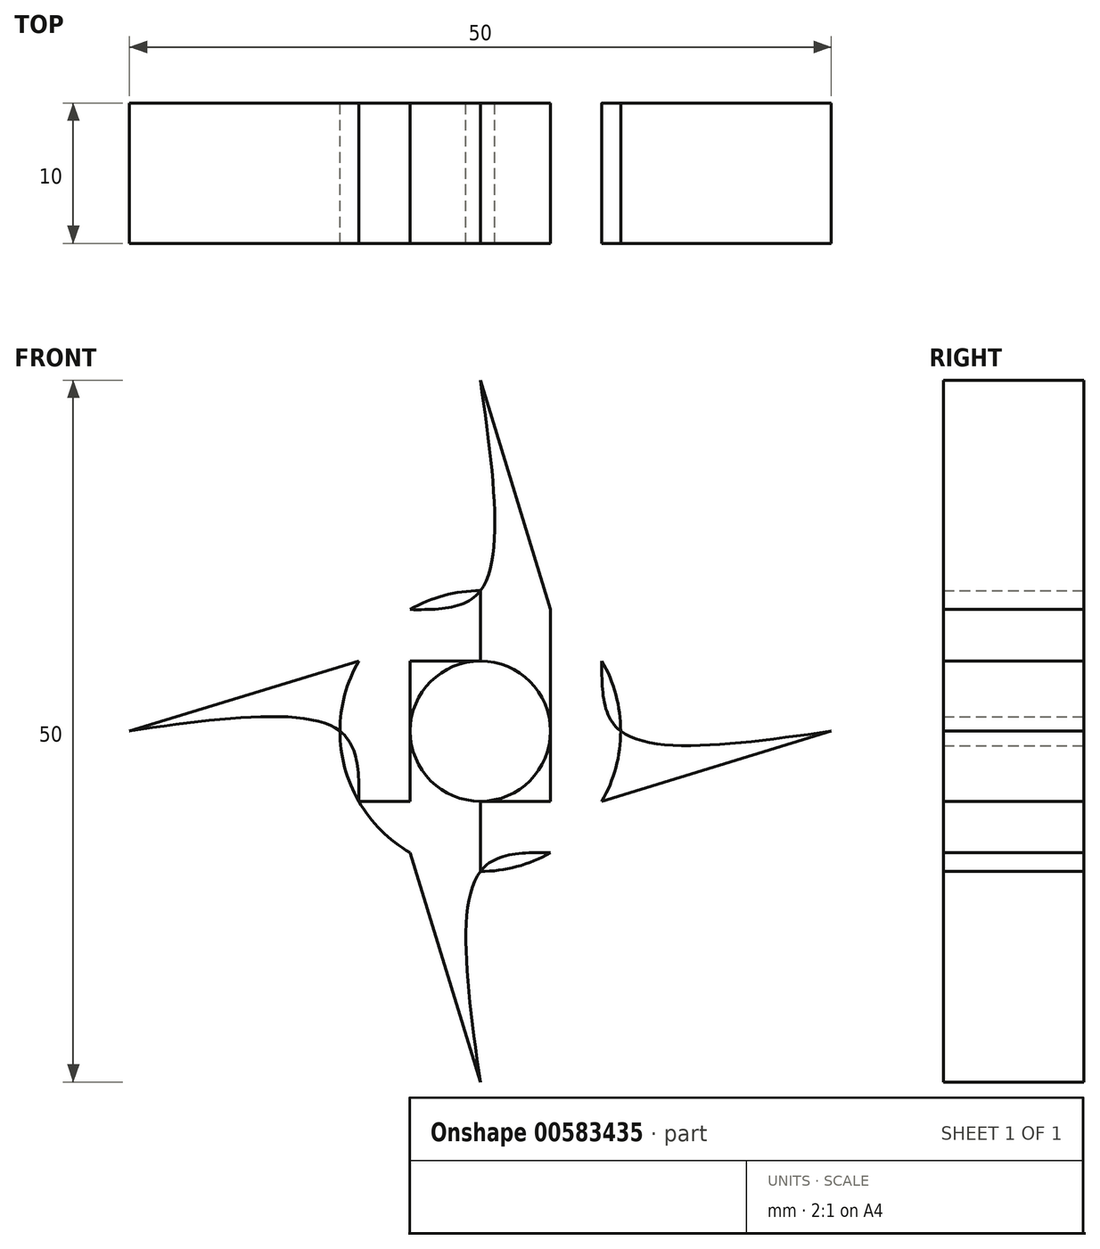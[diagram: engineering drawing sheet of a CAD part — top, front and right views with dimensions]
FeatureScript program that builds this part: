
annotation { "Feature Type Name" : "Feature", "Feature Type Description" : "" }
export const myFeature = defineFeature(function(context is Context, id is Id, definition is map)
    precondition{}
    {
        {
            var Q0;
            Q0=qCreatedBy(makeId("Front.planeOp"),FACE);
            var sketch = newSketch(context, id + "F0", { "sketchPlane" : qUnion([Q0])});
            skCircle(sketch, "E0", {"center": v(0, 0) * mm, "radius": 10 * mm});
            skLineSegment(sketch, "E1", {"start": v(0, 0) * mm, "end": v(0, 10) * mm});
            skLineSegment(sketch, "E2", {"start": v(0, 10) * mm, "end": v(0, -10) * mm});
            skLineSegment(sketch, "E3", {"start": v(-10, 0) * mm, "end": v(10, 0) * mm});
            skLineSegment(sketch, "E4", {"start": v(0, 0) * mm, "end": v(0, -10) * mm});
            skLineSegment(sketch, "E5", {"start": v(0, 0) * mm, "end": v(-10, 0) * mm});
            skLineSegment(sketch, "E6", {"start": v(0, 0) * mm, "end": v(10, 0) * mm});
            skLineSegment(sketch, "E7", {"start": v(0, 5) * mm, "end": v(-8.66, 5) * mm});
            skLineSegment(sketch, "E8", {"start": v(-8.66, 5) * mm, "end": v(8.66, 5) * mm});
            skLineSegment(sketch, "E9", {"start": v(0, -5) * mm, "end": v(8.66, -5) * mm});
            skLineSegment(sketch, "E10", {"start": v(8.66, -5) * mm, "end": v(-8.66, -5) * mm});
            skLineSegment(sketch, "E11", {"start": v(-5, 0) * mm, "end": v(-5, 8.66) * mm});
            skLineSegment(sketch, "E12", {"start": v(-5, 8.66) * mm, "end": v(-5, -8.66) * mm});
            skLineSegment(sketch, "E13", {"start": v(5, 0) * mm, "end": v(5, 8.66) * mm});
            skLineSegment(sketch, "E14", {"start": v(5, 8.66) * mm, "end": v(5, -8.66) * mm});
            skLineSegment(sketch, "E15", {"start": v(-8.66, 5) * mm, "end": v(-5, 5) * mm});
            skLineSegment(sketch, "E16", {"start": v(-5, 5) * mm, "end": v(-5, -5) * mm});
            skLineSegment(sketch, "E17", {"start": v(5, 5) * mm, "end": v(5, -5) * mm});
            skLineSegment(sketch, "E18.bottom", {"start": v(-5, -5) * mm, "end": v(4.96, -5) * mm});
            skLineSegment(sketch, "E19.left", {"start": v(-5, 5) * mm, "end": v(-5, -4.96) * mm});
            skLineSegment(sketch, "E20.bottom", {"start": v(-5, 5) * mm, "end": v(4.96, 5) * mm});
            skLineSegment(sketch, "E21.left", {"start": v(5, 5) * mm, "end": v(5, -4.96) * mm});
            skCircle(sketch, "E22", {"center": v(0, 0) * mm, "radius": 5 * mm});
            skLineSegment(sketch, "E23", {"start": v(25, 0) * mm, "end": v(8.66, -5) * mm});
            skLineSegment(sketch, "E24", {"start": v(-5, -8.66) * mm, "end": v(0, -25) * mm});
            skLineSegment(sketch, "E25", {"start": v(-8.66, 5) * mm, "end": v(-25, 0.02) * mm});
            skLineSegment(sketch, "E26", {"start": v(5, 8.66) * mm, "end": v(0, 25) * mm});
            skFitSpline(sketch, "E27", {"points": [v(0, 25) * mm, v(0, 10) * mm, v(-5, 8.66) * mm], "startDerivative": vector(4.26, -30.17) * mm, "endDerivative": vector(-16.01, 0.12) * mm});
            skFitSpline(sketch, "E28", {"points": [v(25, 0) * mm, v(10, 0) * mm, v(8.66, 5) * mm], "startDerivative": vector(-30.17, -4.26) * mm, "endDerivative": vector(0.12, 16.01) * mm});
            skFitSpline(sketch, "E29", {"points": [v(0, -25) * mm, v(0, -10) * mm, v(5, -8.66) * mm], "startDerivative": vector(-4.26, 30.17) * mm, "endDerivative": vector(16.01, -0.12) * mm});
            skFitSpline(sketch, "E30", {"points": [v(-25, 0.02) * mm, v(-10, 0) * mm, v(-8.66, -5) * mm], "startDerivative": vector(30.17, 4.21) * mm, "endDerivative": vector(-0.12, -16) * mm});
            skSolve(sketch);
        }
        {
            var Q0;
            {var subQ0=sQuery(id+"F0.wireOp",EDGE,"E4");var subQ1=sQuery(id+"F0.wireOp",EDGE,"E0");var subQ2=makeQuery(id+"F0.imprint","INTERSECT",VERTEX,{"derivedFrom":[subQ1,subQ0,sQuery(id+"F0.wireOp",EDGE,"ecfeab35-740d-4c83-b78b-e443c0464c7e")]});Q0=makeQuery(id+"F0.imprint","IMPRINT",FACE,{"disambiguationData":[TD([[makeQuery(id+"F0.imprint","IMPRINT",EDGE,{"disambiguationData":[TD([[subQ2,1.0]])],"derivedFrom":subQ1}),1.0]])]});}
            var Q1;
            {var subQ0=sQuery(id+"F0.wireOp",EDGE,"ecfeab35-740d-4c83-b78b-e443c0464c7e");var subQ1=sQuery(id+"F0.wireOp",EDGE,"E4");var subQ2=sQuery(id+"F0.wireOp",EDGE,"E0");var subQ3=makeQuery(id+"F0.imprint","INTERSECT",VERTEX,{"derivedFrom":[subQ2,subQ1,subQ0]});Q1=makeQuery(id+"F0.imprint","IMPRINT",FACE,{"disambiguationData":[TD([[makeQuery(id+"F0.imprint","IMPRINT",EDGE,{"disambiguationData":[TD([[subQ3,1.0]])],"derivedFrom":subQ1}),1.0]])]});}
            var Q2;
            {var subQ0=sQuery(id+"F0.wireOp",EDGE,"E10");var subQ1=sQuery(id+"F0.wireOp",EDGE,"E0");var subQ2=makeQuery(id+"F0.imprint","INTERSECT",VERTEX,{"derivedFrom":[subQ1,subQ0,sQuery(id+"F0.wireOp",EDGE,"sRVM3hvw-lM5L-FAK7-h2Cm-fDXYcMHcet7f")]});Q2=makeQuery(id+"F0.imprint","IMPRINT",FACE,{"disambiguationData":[TD([[makeQuery(id+"F0.imprint","IMPRINT",EDGE,{"disambiguationData":[TD([[subQ2,1.0]])],"derivedFrom":subQ1}),1.0]])]});}
            var Q3;
            {var subQ0=sQuery(id+"F0.wireOp",EDGE,"E6");var subQ1=sQuery(id+"F0.wireOp",EDGE,"E0");var subQ2=makeQuery(id+"F0.imprint","INTERSECT",VERTEX,{"derivedFrom":[subQ1,subQ0,sQuery(id+"F0.wireOp",EDGE,"dcaebb9e-91c8-481a-8361-05b1eb6cbfa7")]});Q3=makeQuery(id+"F0.imprint","IMPRINT",FACE,{"disambiguationData":[TD([[makeQuery(id+"F0.imprint","IMPRINT",EDGE,{"disambiguationData":[TD([[subQ2,1.0]])],"derivedFrom":subQ1}),1.0]])]});}
            var Q4;
            {var subQ6=sQuery(id+"F0.wireOp",EDGE,"E8");Q4=makeQuery(id+"F0.imprint","IMPRINT",FACE,{"disambiguationData":[TD([[makeQuery(id+"F0.imprint","IMPRINT",EDGE,{"derivedFrom":subQ6}),-1.0]])]});}
            var Q5;
            {var subQ0=sQuery(id+"F0.wireOp",EDGE,"E8");Q5=makeQuery(id+"F0.imprint","IMPRINT",FACE,{"disambiguationData":[TD([[makeQuery(id+"F0.imprint","IMPRINT",EDGE,{"derivedFrom":subQ0}),1.0]])]});}
            var Q6;
            {var subQ0=sQuery(id+"F0.wireOp",EDGE,"E2");var subQ1=sQuery(id+"F0.wireOp",EDGE,"E0");var subQ2=makeQuery(id+"F0.imprint","INTERSECT",VERTEX,{"derivedFrom":[subQ1,subQ0,sQuery(id+"F0.wireOp",EDGE,"3b5c119a-1b97-4d2e-8cfb-29280de54832")]});Q6=makeQuery(id+"F0.imprint","IMPRINT",FACE,{"disambiguationData":[TD([[makeQuery(id+"F0.imprint","IMPRINT",EDGE,{"disambiguationData":[TD([[subQ2,1.0]])],"derivedFrom":subQ1}),1.0]])]});}
            var Q7;
            {var subQ0=sQuery(id+"F0.wireOp",EDGE,"3b5c119a-1b97-4d2e-8cfb-29280de54832");var subQ1=sQuery(id+"F0.wireOp",EDGE,"E2");var subQ2=sQuery(id+"F0.wireOp",EDGE,"E0");var subQ3=makeQuery(id+"F0.imprint","INTERSECT",VERTEX,{"derivedFrom":[subQ2,subQ1,subQ0]});Q7=makeQuery(id+"F0.imprint","IMPRINT",FACE,{"disambiguationData":[TD([[makeQuery(id+"F0.imprint","IMPRINT",EDGE,{"disambiguationData":[TD([[subQ3,-1.0]])],"derivedFrom":subQ1}),-1.0]])]});}
            var Q8;
            {var subQ3=sQuery(id+"F0.wireOp",EDGE,"E15");Q8=makeQuery(id+"F0.imprint","IMPRINT",FACE,{"disambiguationData":[TD([[makeQuery(id+"F0.imprint","IMPRINT",EDGE,{"derivedFrom":subQ3}),-1.0]])]});}
            var Q9;
            {var subQ0=sQuery(id+"F0.wireOp",EDGE,"a55a1d35-224c-42bd-bfe0-43a0404cdbfa");var subQ1=sQuery(id+"F0.wireOp",EDGE,"E5");var subQ2=sQuery(id+"F0.wireOp",EDGE,"E0");var subQ3=makeQuery(id+"F0.imprint","INTERSECT",VERTEX,{"derivedFrom":[subQ2,subQ1,subQ0]});Q9=makeQuery(id+"F0.imprint","IMPRINT",FACE,{"disambiguationData":[TD([[makeQuery(id+"F0.imprint","IMPRINT",EDGE,{"disambiguationData":[TD([[subQ3,1.0]])],"derivedFrom":subQ1}),1.0]])]});}
            var Q10;
            {var subQ0=sQuery(id+"F0.wireOp",EDGE,"E10");var subQ1=sQuery(id+"F0.wireOp",EDGE,"E0");var subQ2=makeQuery(id+"F0.imprint","INTERSECT",VERTEX,{"derivedFrom":[subQ1,subQ0,sQuery(id+"F0.wireOp",EDGE,"a55a1d35-224c-42bd-bfe0-43a0404cdbfa")]});Q10=makeQuery(id+"F0.imprint","IMPRINT",FACE,{"disambiguationData":[TD([[makeQuery(id+"F0.imprint","IMPRINT",EDGE,{"disambiguationData":[TD([[subQ2,-1.0]])],"derivedFrom":subQ1}),1.0]])]});}
            var Q11;
            {var subQ3=sQuery(id+"F0.wireOp",EDGE,"E15");Q11=makeQuery(id+"F0.imprint","IMPRINT",FACE,{"disambiguationData":[TD([[makeQuery(id+"F0.imprint","IMPRINT",EDGE,{"derivedFrom":subQ3}),1.0]])]});}
            var Q12;
            {var subQ0=sQuery(id+"F0.wireOp",EDGE,"ecfeab35-740d-4c83-b78b-e443c0464c7e");var subQ1=sQuery(id+"F0.wireOp",EDGE,"E0");var subQ2=makeQuery(id+"F0.imprint","INTERSECT",VERTEX,{"derivedFrom":[subQ1,sQuery(id+"F0.wireOp",EDGE,"E4"),subQ0]});Q12=makeQuery(id+"F0.imprint","IMPRINT",FACE,{"disambiguationData":[TD([[makeQuery(id+"F0.imprint","IMPRINT",EDGE,{"disambiguationData":[TD([[subQ2,-1.0]])],"derivedFrom":subQ1}),1.0]])]});}
            var Q13;
            {var subQ0=sQuery(id+"F0.wireOp",EDGE,"a55a1d35-224c-42bd-bfe0-43a0404cdbfa");var subQ1=sQuery(id+"F0.wireOp",EDGE,"E0");var subQ2=makeQuery(id+"F0.imprint","INTERSECT",VERTEX,{"derivedFrom":[subQ1,sQuery(id+"F0.wireOp",EDGE,"E5"),subQ0]});Q13=makeQuery(id+"F0.imprint","IMPRINT",FACE,{"disambiguationData":[TD([[makeQuery(id+"F0.imprint","IMPRINT",EDGE,{"disambiguationData":[TD([[subQ2,-1.0]])],"derivedFrom":subQ1}),1.0]])]});}
            var Q14;
            {var subQ0=sQuery(id+"F0.wireOp",EDGE,"dcaebb9e-91c8-481a-8361-05b1eb6cbfa7");var subQ1=sQuery(id+"F0.wireOp",EDGE,"E0");var subQ2=makeQuery(id+"F0.imprint","INTERSECT",VERTEX,{"derivedFrom":[subQ1,sQuery(id+"F0.wireOp",EDGE,"E6"),subQ0]});Q14=makeQuery(id+"F0.imprint","IMPRINT",FACE,{"disambiguationData":[TD([[makeQuery(id+"F0.imprint","IMPRINT",EDGE,{"disambiguationData":[TD([[subQ2,-1.0]])],"derivedFrom":subQ1}),1.0]])]});}
            var Q15;
            {var subQ0=sQuery(id+"F0.wireOp",EDGE,"3b5c119a-1b97-4d2e-8cfb-29280de54832");var subQ1=sQuery(id+"F0.wireOp",EDGE,"E0");var subQ2=makeQuery(id+"F0.imprint","INTERSECT",VERTEX,{"derivedFrom":[subQ1,sQuery(id+"F0.wireOp",EDGE,"E2"),subQ0]});Q15=makeQuery(id+"F0.imprint","IMPRINT",FACE,{"disambiguationData":[TD([[makeQuery(id+"F0.imprint","IMPRINT",EDGE,{"disambiguationData":[TD([[subQ2,-1.0]])],"derivedFrom":subQ1}),1.0]])]});}
            var Q16;
            {var subQ1=sQuery(id+"F0.wireOp",EDGE,"E18.bottom");var subQ3=sQuery(id+"F0.wireOp",EDGE,"E22");var subQ4=makeQuery(id+"F0.imprint","INTERSECT",VERTEX,{"derivedFrom":[sQuery(id+"F0.wireOp",EDGE,"E4"),subQ1,subQ3]});Q16=makeQuery(id+"F0.imprint","IMPRINT",FACE,{"disambiguationData":[TD([[makeQuery(id+"F0.imprint","IMPRINT",EDGE,{"disambiguationData":[TD([[subQ4,1.0]])],"derivedFrom":subQ3}),-1.0]])]});}
            var Q17;
            {var subQ0=sQuery(id+"F0.wireOp",EDGE,"E20.bottom");var subQ3=sQuery(id+"F0.wireOp",EDGE,"E22");var subQ5=makeQuery(id+"F0.imprint","INTERSECT",VERTEX,{"derivedFrom":[sQuery(id+"F0.wireOp",EDGE,"E2"),subQ0,subQ3]});Q17=makeQuery(id+"F0.imprint","IMPRINT",FACE,{"disambiguationData":[TD([[makeQuery(id+"F0.imprint","IMPRINT",EDGE,{"disambiguationData":[TD([[subQ5,-1.0]])],"derivedFrom":subQ3}),-1.0]])]});}
            var Q18;
            {var subQ1=sQuery(id+"F0.wireOp",EDGE,"E20.bottom");var subQ3=sQuery(id+"F0.wireOp",EDGE,"E22");var subQ4=makeQuery(id+"F0.imprint","INTERSECT",VERTEX,{"derivedFrom":[sQuery(id+"F0.wireOp",EDGE,"E2"),subQ1,subQ3]});Q18=makeQuery(id+"F0.imprint","IMPRINT",FACE,{"disambiguationData":[TD([[makeQuery(id+"F0.imprint","IMPRINT",EDGE,{"disambiguationData":[TD([[subQ4,1.0]])],"derivedFrom":subQ3}),-1.0]])]});}
            var Q19;
            {var subQ1=sQuery(id+"F0.wireOp",EDGE,"E18.bottom");var subQ3=sQuery(id+"F0.wireOp",EDGE,"E22");var subQ4=makeQuery(id+"F0.imprint","INTERSECT",VERTEX,{"derivedFrom":[sQuery(id+"F0.wireOp",EDGE,"E4"),subQ1,subQ3]});Q19=makeQuery(id+"F0.imprint","IMPRINT",FACE,{"disambiguationData":[TD([[makeQuery(id+"F0.imprint","IMPRINT",EDGE,{"disambiguationData":[TD([[subQ4,-1.0]])],"derivedFrom":subQ3}),-1.0]])]});}
            var Q20;
            {var subQ3=sQuery(id+"F0.wireOp",EDGE,"AYTwL2iG-ZeRN-Ob4u-AX6t-Utk9oqFyEy4r");Q20=makeQuery(id+"F0.imprint","IMPRINT",FACE,{"disambiguationData":[TD([[makeQuery(id+"F0.imprint","IMPRINT",EDGE,{"derivedFrom":subQ3}),-1.0]])]});}
            var Q21;
            {var subQ3=sQuery(id+"F0.wireOp",EDGE,"yNIuoGms-5zRm-s3Bl-2k3e-Q7XeYXnXF8j0");Q21=makeQuery(id+"F0.imprint","IMPRINT",FACE,{"disambiguationData":[TD([[makeQuery(id+"F0.imprint","IMPRINT",EDGE,{"derivedFrom":subQ3}),1.0]])]});}
            var Q22;
            {var subQ3=sQuery(id+"F0.wireOp",EDGE,"w7b3tdaU-Tdgz-wxAI-8haA-Ab0gXEcMYndZ");Q22=makeQuery(id+"F0.imprint","IMPRINT",FACE,{"disambiguationData":[TD([[makeQuery(id+"F0.imprint","IMPRINT",EDGE,{"derivedFrom":subQ3}),-1.0]])]});}
            var Q23;
            {var subQ3=sQuery(id+"F0.wireOp",EDGE,"sRVM3hvw-lM5L-FAK7-h2Cm-fDXYcMHcet7f");Q23=makeQuery(id+"F0.imprint","IMPRINT",FACE,{"disambiguationData":[TD([[makeQuery(id+"F0.imprint","IMPRINT",EDGE,{"derivedFrom":subQ3}),-1.0]])]});}
            var Q24;
            {var subQ0=sQuery(id+"F0.wireOp",EDGE,"E10");var subQ1=sQuery(id+"F0.wireOp",EDGE,"E0");var subQ2=makeQuery(id+"F0.imprint","INTERSECT",VERTEX,{"derivedFrom":[subQ1,subQ0,sQuery(id+"F0.wireOp",EDGE,"E23")]});Q24=makeQuery(id+"F0.imprint","IMPRINT",FACE,{"disambiguationData":[TD([[makeQuery(id+"F0.imprint","IMPRINT",EDGE,{"disambiguationData":[TD([[subQ2,1.0]])],"derivedFrom":subQ1}),1.0]])]});}
            var Q25;
            {var subQ3=sQuery(id+"F0.wireOp",EDGE,"E23");Q25=makeQuery(id+"F0.imprint","IMPRINT",FACE,{"disambiguationData":[TD([[makeQuery(id+"F0.imprint","IMPRINT",EDGE,{"derivedFrom":subQ3}),-1.0]])]});}
            var Q26;
            {var subQ3=sQuery(id+"F0.wireOp",EDGE,"E26");Q26=makeQuery(id+"F0.imprint","IMPRINT",FACE,{"disambiguationData":[TD([[makeQuery(id+"F0.imprint","IMPRINT",EDGE,{"derivedFrom":subQ3}),1.0]])]});}
            var Q27;
            {var subQ3=sQuery(id+"F0.wireOp",EDGE,"E25");Q27=makeQuery(id+"F0.imprint","IMPRINT",FACE,{"disambiguationData":[TD([[makeQuery(id+"F0.imprint","IMPRINT",EDGE,{"derivedFrom":subQ3}),1.0]])]});}
            var Q28;
            {var subQ3=sQuery(id+"F0.wireOp",EDGE,"E24");Q28=makeQuery(id+"F0.imprint","IMPRINT",FACE,{"disambiguationData":[TD([[makeQuery(id+"F0.imprint","IMPRINT",EDGE,{"derivedFrom":subQ3}),1.0]])]});}
            extrude(context, id + "F1", {"entities" : qUnion([Q0, Q1, Q2, Q3, Q4, Q5, Q6, Q7, Q8, Q9, Q10, Q11, Q12, Q13, Q14, Q15, Q16, Q17, Q18, Q19, Q20, Q21, Q22, Q23, Q24, Q25, Q26, Q27, Q28]), "depth" : 10 * mm, "offsetDistance" : 25 * mm});
        }
    });
